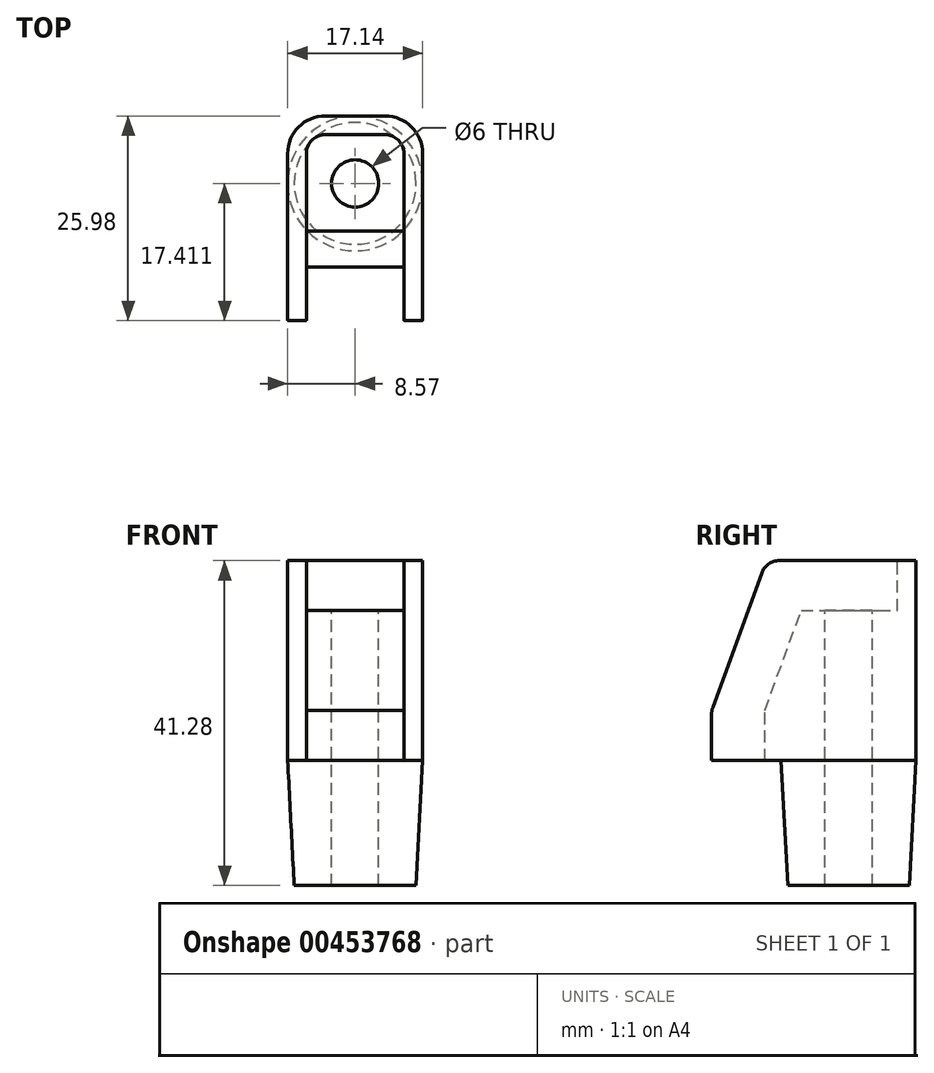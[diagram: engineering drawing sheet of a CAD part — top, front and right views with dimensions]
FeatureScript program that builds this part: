
annotation { "Feature Type Name" : "Feature", "Feature Type Description" : "" }
export const myFeature = defineFeature(function(context is Context, id is Id, definition is map)
    precondition{}
    {
        {
            var Q0;
            Q0=qCreatedBy(makeId("Right.planeOp"),FACE);
            var sketch = newSketch(context, id + "F0", { "sketchPlane" : qUnion([Q0])});
            skLineSegment(sketch, "E0.bottom", {"start": v(0, 0) * mm, "end": v(25.98, 0) * mm});
            skLineSegment(sketch, "E0.top", {"start": v(6.93, 19.05) * mm, "end": v(25.98, 19.05) * mm});
            skLineSegment(sketch, "E0.right", {"start": v(25.98, 0) * mm, "end": v(25.98, 19.05) * mm});
            skLineSegment(sketch, "E1", {"start": v(0, 0) * mm, "end": v(6.93, 19.05) * mm});
            skSolve(sketch);
        }
        {
            var Q0;
            Q0 = qSketchRegion(id + "F0", true);
            extrude(context, id + "F1", {"entities" : qUnion([Q0]), "endBound" : BoundingType.SYMMETRIC, "depth" : 17.14 * mm});
        }
        {
            var Q0;
            Q0=makeQuery(id+"F1.opExtrude","SWEPT_FACE",FACE,{"disambiguationData":[OSD([sQuery(id+"F0.wireOp",EDGE,"E1")])]});
            var sketch = newSketch(context, id + "F2", { "sketchPlane" : qUnion([Q0])});
            skLineSegment(sketch, "E2.bottom", {"start": v(6.18, -2.54) * mm, "end": v(-6.2, -2.54) * mm});
            skLineSegment(sketch, "E2.top", {"start": v(6.18, 22.81) * mm, "end": v(-6.2, 22.81) * mm});
            skLineSegment(sketch, "E2.left", {"start": v(6.18, -2.54) * mm, "end": v(6.18, 22.81) * mm});
            skLineSegment(sketch, "E2.right", {"start": v(-6.2, -2.54) * mm, "end": v(-6.2, 22.81) * mm});
            skSolve(sketch);
        }
        {
            var Q0;
            Q0=makeQuery(id+"F1.opExtrude","SWEPT_FACE",FACE,{"disambiguationData":[OSD([sQuery(id+"F0.wireOp",EDGE,"E0.top")])]});
            var sketch = newSketch(context, id + "F3", { "sketchPlane" : qUnion([Q0])});
            skLineSegment(sketch, "E3.bottom", {"start": v(-6.2, 4.4) * mm, "end": v(6.2, 4.4) * mm});
            skLineSegment(sketch, "E3.left", {"start": v(-6.2, 4.4) * mm, "end": v(-6.2, 23.6) * mm});
            skLineSegment(sketch, "E3.right", {"start": v(6.2, 4.4) * mm, "end": v(6.2, 23.6) * mm});
            skLineSegment(sketch, "E4", {"start": v(-6.2, 23.6) * mm, "end": v(6.2, 23.6) * mm});
            skSolve(sketch);
        }
        {
            var Q0;
            Q0 = qSketchRegion(id + "F2", true);
            extrude(context, id + "F4", {"entities" : qUnion([Q0]), "operationType" : NewBodyOperationType.REMOVE, "oppositeDirection" : true, "depth" : 6.35 * mm});
        }
        {
            var Q0;
            Q0 = qSketchRegion(id + "F3", true);
            extrude(context, id + "F5", {"entities" : qUnion([Q0]), "operationType" : NewBodyOperationType.REMOVE, "oppositeDirection" : true, "depth" : 6.35 * mm});
        }
        {
            var Q0;
            Q0=makeQuery(id+"F1.opExtrude","SWEPT_FACE",FACE,{"disambiguationData":[OSD([sQuery(id+"F0.wireOp",EDGE,"E0.bottom")])]});
            var sketch = newSketch(context, id + "F6", { "sketchPlane" : qUnion([Q0])});
            skLineSegment(sketch, "E5.bottom", {"start": v(-8.57, -25.98) * mm, "end": v(8.57, -25.98) * mm});
            skLineSegment(sketch, "E5.top", {"start": v(-8.57, 0) * mm, "end": v(-6.2, 0) * mm});
            skLineSegment(sketch, "E5.left", {"start": v(-8.57, -25.98) * mm, "end": v(-8.57, 0) * mm});
            skLineSegment(sketch, "E5.right", {"start": v(8.57, -25.98) * mm, "end": v(8.57, 0) * mm});
            skLineSegment(sketch, "E6.bottom", {"start": v(-6.2, -6.76) * mm, "end": v(6.18, -6.76) * mm});
            skLineSegment(sketch, "E6.left", {"start": v(-6.2, -6.76) * mm, "end": v(-6.2, 0) * mm});
            skLineSegment(sketch, "E6.right", {"start": v(6.18, -6.76) * mm, "end": v(6.18, 0) * mm});
            skLineSegment(sketch, "E7.trimOffspring", {"start": v(6.18, 0) * mm, "end": v(8.57, 0) * mm});
            skSolve(sketch);
        }
        {
            var Q0;
            Q0 = qSketchRegion(id + "F6", true);
            extrude(context, id + "F7", {"entities" : qUnion([Q0]), "operationType" : NewBodyOperationType.ADD, "depth" : 6.35 * mm});
        }
        {
            var Q0;
            {var subQ0=sQuery(id+"F0.wireOp",EDGE,"E0.bottom");var subQ1=sQuery(id+"F0.wireOp",EDGE,"E1");Q0=makeQuery(id+"F7.boolean.opBoolean","MERGE",EDGE,{"derivedFrom":[makeQuery(id+"F4.boolean.opBoolean","SPLIT",EDGE,{"disambiguationData":[TD([makeQuery(id+"F4.opExtrude","SWEPT_FACE",FACE,{"disambiguationData":[OSD([sQuery(id+"F2.wireOp",EDGE,"E2.right")])]})])],"derivedFrom":makeQuery(id+"F1.opExtrude","SWEPT_EDGE",EDGE,{"disambiguationData":[OSD([subQ0,subQ1])]})}),makeQuery(id+"F7.opExtrude","CAP_EDGE",EDGE,{"disambiguationData":[OSD([sQuery(id+"F6.wireOp",EDGE,"E5.top")])],"isStart":true})]});}
            var Q1;
            {var subQ0=sQuery(id+"F0.wireOp",EDGE,"E0.bottom");var subQ1=sQuery(id+"F0.wireOp",EDGE,"E1");Q1=makeQuery(id+"F7.boolean.opBoolean","MERGE",EDGE,{"derivedFrom":[makeQuery(id+"F4.boolean.opBoolean","SPLIT",EDGE,{"disambiguationData":[TD([makeQuery(id+"F4.opExtrude","SWEPT_FACE",FACE,{"disambiguationData":[OSD([sQuery(id+"F2.wireOp",EDGE,"E2.left")])]})])],"derivedFrom":makeQuery(id+"F1.opExtrude","SWEPT_EDGE",EDGE,{"disambiguationData":[OSD([subQ0,subQ1])]})}),makeQuery(id+"F7.opExtrude","CAP_EDGE",EDGE,{"disambiguationData":[OSD([sQuery(id+"F6.wireOp",EDGE,"E7.trimOffspring")])],"isStart":true})]});}
            var Q2;
            {var subQ0=sQuery(id+"F0.wireOp",EDGE,"E1");var subQ1=sQuery(id+"F0.wireOp",EDGE,"E0.top");Q2=makeQuery(id+"F4.boolean.opBoolean","SPLIT",EDGE,{"disambiguationData":[TD([makeQuery(id+"F4.opExtrude","SWEPT_FACE",FACE,{"disambiguationData":[OSD([sQuery(id+"F2.wireOp",EDGE,"E2.right")])]})])],"derivedFrom":makeQuery(id+"F1.opExtrude","SWEPT_EDGE",EDGE,{"disambiguationData":[OSD([subQ1,subQ0])]})});}
            var Q3;
            {var subQ0=sQuery(id+"F0.wireOp",EDGE,"E1");var subQ1=sQuery(id+"F0.wireOp",EDGE,"E0.top");Q3=makeQuery(id+"F4.boolean.opBoolean","SPLIT",EDGE,{"disambiguationData":[TD([makeQuery(id+"F4.opExtrude","SWEPT_FACE",FACE,{"disambiguationData":[OSD([sQuery(id+"F2.wireOp",EDGE,"E2.left")])]})])],"derivedFrom":makeQuery(id+"F1.opExtrude","SWEPT_EDGE",EDGE,{"disambiguationData":[OSD([subQ1,subQ0])]})});}
            var Q4;
            Q4=makeQuery(id+"F5.boolean.opBoolean","COPY",EDGE,{"derivedFrom":makeQuery(id+"F5.opExtrude","SWEPT_EDGE",EDGE,{"disambiguationData":[OSD([sQuery(id+"F3.wireOp",EDGE,"E3.left"),sQuery(id+"F3.wireOp",EDGE,"E4")])]})});
            var Q5;
            Q5=makeQuery(id+"F5.boolean.opBoolean","COPY",EDGE,{"derivedFrom":makeQuery(id+"F5.opExtrude","SWEPT_EDGE",EDGE,{"disambiguationData":[OSD([sQuery(id+"F3.wireOp",EDGE,"E3.right"),sQuery(id+"F3.wireOp",EDGE,"E4")])]})});
            fillet(context, id + "F8", {"entities" : qUnion([Q0, Q1, Q2, Q3, Q4, Q5]), "radius" : 2.38 * mm, "tangentPropagation" : true, "allowEdgeOverflow" : false});
        }
        {
            var Q0;
            Q0=makeQuery(id+"F7.boolean.opBoolean","MERGE",EDGE,{"derivedFrom":[makeQuery(id+"F1.opExtrude","CAP_EDGE",EDGE,{"disambiguationData":[OSD([sQuery(id+"F0.wireOp",EDGE,"E0.right")])],"isStart":true}),makeQuery(id+"F7.opExtrude","SWEPT_EDGE",EDGE,{"disambiguationData":[OSD([sQuery(id+"F6.wireOp",EDGE,"E5.bottom"),sQuery(id+"F6.wireOp",EDGE,"E5.left")])]})]});
            var Q1;
            Q1=makeQuery(id+"F7.boolean.opBoolean","MERGE",EDGE,{"derivedFrom":[makeQuery(id+"F1.opExtrude","CAP_EDGE",EDGE,{"disambiguationData":[OSD([sQuery(id+"F0.wireOp",EDGE,"E0.right")])],"isStart":false}),makeQuery(id+"F7.opExtrude","SWEPT_EDGE",EDGE,{"disambiguationData":[OSD([sQuery(id+"F6.wireOp",EDGE,"E5.bottom"),sQuery(id+"F6.wireOp",EDGE,"E5.right")])]})]});
            fillet(context, id + "F9", {"entities" : qUnion([Q0, Q1]), "radius" : 4.76 * mm, "tangentPropagation" : true, "allowEdgeOverflow" : false});
        }
        {
            var Q0;
            Q0=makeQuery(id+"F7.opExtrude","CAP_FACE",FACE,{"disambiguationData":[OSD([sQuery(id+"F6.wireOp",EDGE,"E5.bottom"),sQuery(id+"F6.wireOp",EDGE,"E5.top"),sQuery(id+"F6.wireOp",EDGE,"E5.left"),sQuery(id+"F6.wireOp",EDGE,"E5.right"),sQuery(id+"F6.wireOp",EDGE,"E6.bottom"),sQuery(id+"F6.wireOp",EDGE,"E6.left"),sQuery(id+"F6.wireOp",EDGE,"E6.right"),sQuery(id+"F6.wireOp",EDGE,"E7.trimOffspring")])],"isStart":false});
            var sketch = newSketch(context, id + "F10", { "sketchPlane" : qUnion([Q0])});
            skCircle(sketch, "E8", {"center": v(0, -17.41) * mm, "radius": 8.57 * mm});
            skSolve(sketch);
        }
        {
            var Q0;
            Q0 = qSketchRegion(id + "F10", true);
            extrude(context, id + "F11", {"entities" : qUnion([Q0]), "operationType" : NewBodyOperationType.ADD, "depth" : 15.88 * mm, "hasDraft" : true, "draftAngle" : 3 * degree, "draftPullDirection" : true});
        }
        {
            var Q0;
            Q0=makeQuery(id+"F5.boolean.opBoolean","COPY",FACE,{"derivedFrom":makeQuery(id+"F5.opExtrude","CAP_FACE",FACE,{"disambiguationData":[OSD([sQuery(id+"F3.wireOp",EDGE,"E3.bottom"),sQuery(id+"F3.wireOp",EDGE,"E3.left"),sQuery(id+"F3.wireOp",EDGE,"E3.right"),sQuery(id+"F3.wireOp",EDGE,"E4")])],"isStart":false})});
            var sketch = newSketch(context, id + "F12", { "sketchPlane" : qUnion([Q0])});
            skCircle(sketch, "E9", {"center": v(0, 17.41) * mm, "radius": 6.2 * mm, "construction": true});
            skCircle(sketch, "E10", {"center": v(0, 17.41) * mm, "radius": 3 * mm});
            skSolve(sketch);
        }
        {
            var Q0;
            Q0 = qSketchRegion(id + "F12", true);
            extrude(context, id + "F13", {"entities" : qUnion([Q0]), "operationType" : NewBodyOperationType.REMOVE, "endBound" : BoundingType.THROUGH_ALL, "oppositeDirection" : true, "depth" : 7.62 * mm});
        }
    });
